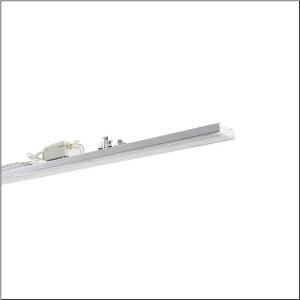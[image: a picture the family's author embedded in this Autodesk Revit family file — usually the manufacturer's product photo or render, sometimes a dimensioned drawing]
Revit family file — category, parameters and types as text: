
# Revit family: licross_r__21_recessed_ho_52tl12dn4fxm3s_7ef7
name_source: partatom
category: Lighting Fixtures
units: mm (PartAtom-declared; Revit-internal decimal feet)

## family parameters
Cut with Voids When Loaded = No
Host = Face
Light Source = No
Part Type = Normal
Room Calculation Point = No
Round Connector Dimension = Use Diameter
Shared = No

## types (1)
- --- (1 x LED, 930 lm, 7.5 W, 4000K)
    Apparent Load = 8 VA
    CIE Flux Codes = 69 91 98 100 100
    Color Rendering = 80
    Color Temperature = 4000K
    Default Elevation = 1800 mm
    Description = Licross® 21 Recessed HO, luminaire insert, of sheet steel, galvanised, coil coated, white, length: 1.500mm, width: 66mm, height: 67mm, LED rated luminous flux: 15.000lm, light colour: 840, control gear: DALI 2, with plug, 6-pole, with phase selection, for trunking rail, 14-core, mains connection: 220..240V, AC, 50/60Hz, rated input power: 88W, halogen-free wiring, for emergency light function, for trunking rail, 14-core, converter,control gear: single battery element, battery: LiFeP04, 9Ah, primary optical cover: cover, of PMMA, light emission: direct distribution, primary light characteristic: symmetric, protection rating (complete): IP40, insulation class (complete): insulation class I (protective earthing), certification: CE, UKCA, protection symbol: D if used in an environment without relevant dust loads with corresponding accessories, impact resistance: IK06, permissible ambient temperature for indoor applications: +5..+30°C, standard: EN 60598-2-22, LABS conformity tested according to VDMA 24364:2018-05, reducing of maximum allowable ambient temperature of 5°C with ceiling mounting, corresponds to IFS (International Featured Standards) requirements for safety and quality in the food industry, packaging unit: 1 piece
    Height = 58 mm
    Lamp = 1 x LED
    Lamp Light Flux = 930 lm
    Lamp Power = 7.5 W
    Lamp count = 1
    Length = 1500 mm
    Luminous efficacy = 124 lm/W
    Manufacturer = Siteco
    ModVariant = No
    Model = 52TL12DN4FXM3S
    Mounting Place = Ceiling
    Mounting Type = Pendant
    Number of Poles = 1
    OnlyDefault = Yes
    Power Factor = 1
    Product Name = Licross® 21 Recessed HO
    Product group = luminaire insert
    ProductGroupID = 901
    Protection Class = Protection class I
    Protection Degree = IP 40
    RLX_Detail_Level = 1
    RLX_Emergency_Light_Flux = 0 lm
    RLX_Emergency_Type = 0
    RLX_Emergency_Type_DB = No
    RlxData = <blob elided: 25141 chars, md5=c95b3f6e>
    Socket = socket
    Standby Power = 0 W
    System Light Flux = 930 lm
    System Power = 8 W
    Type Comments = : emergency light operation: 3 h
    Type Image = l_1296930.jpg
    URL = http://relux.com
    VarID = @adj_039451
    Voltage = 0 V
    Weight = 0.00 kg
    Width = 66 mm

## geometry (parser evidence)
native form markers: Blend x4, Sweep x13
no freeform markers — native parametric forms only
